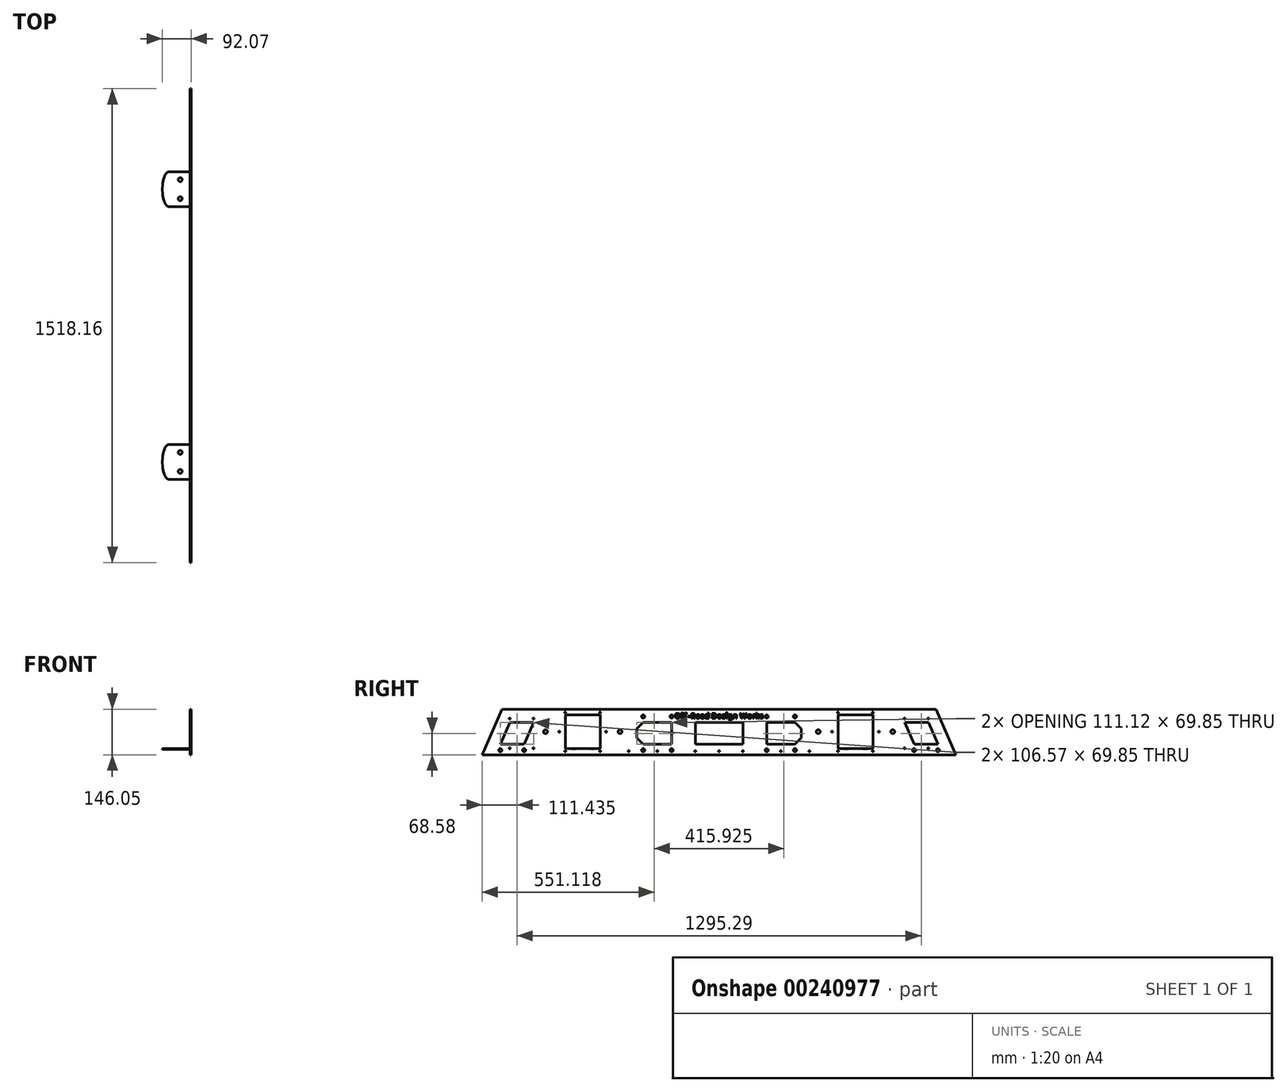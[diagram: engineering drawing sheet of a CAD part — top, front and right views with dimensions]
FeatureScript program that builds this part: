
annotation { "Feature Type Name" : "Feature", "Feature Type Description" : "" }
export const myFeature = defineFeature(function(context is Context, id is Id, definition is map)
    precondition{}
    {
        {
            var Q0;
            Q0=qCreatedBy(makeId("Right.planeOp"),FACE);
            var sketch = newSketch(context, id + "F0", { "sketchPlane" : qUnion([Q0])});
            skLineSegment(sketch, "E0", {"start": v(0, 0) * mm, "end": v(-759.08, 0) * mm});
            skLineSegment(sketch, "E1", {"start": v(-759.08, 0) * mm, "end": v(-695.58, 146.05) * mm});
            skLineSegment(sketch, "E2", {"start": v(-695.58, 146.05) * mm, "end": v(0, 146.05) * mm});
            skLineSegment(sketch, "E3", {"start": v(0, 0) * mm, "end": v(0, 460.36) * mm, "construction": true});
            skLineSegment(sketch, "E4.MirrorCS", {"start": v(695.58, 146.05) * mm, "end": v(0, 146.05) * mm});
            skLineSegment(sketch, "E5.MirrorCS", {"start": v(759.08, 0) * mm, "end": v(695.58, 146.05) * mm});
            skLineSegment(sketch, "E6.MirrorCS", {"start": v(0, 0) * mm, "end": v(759.08, 0) * mm});
            skSolve(sketch);
        }
        {
            var Q0;
            Q0 = qSketchRegion(id + "F0", true);
            extrude(context, id + "F1", {"entities" : qUnion([Q0]), "oppositeDirection" : true, "depth" : 3.17 * mm});
        }
        {
            var Q0;
            Q0=makeQuery(id+"F1.opExtrude","CAP_FACE",FACE,{"disambiguationData":[OSD([sQuery(id+"F0.wireOp",EDGE,"E0"),sQuery(id+"F0.wireOp",EDGE,"E1"),sQuery(id+"F0.wireOp",EDGE,"E2"),sQuery(id+"F0.wireOp",EDGE,"E4.MirrorCS"),sQuery(id+"F0.wireOp",EDGE,"E5.MirrorCS"),sQuery(id+"F0.wireOp",EDGE,"E6.MirrorCS")])],"isStart":true});
            var sketch = newSketch(context, id + "F2", { "sketchPlane" : qUnion([Q0])});
            skLineSegment(sketch, "E7", {"start": v(0, 0) * mm, "end": v(0, 457.35) * mm, "construction": true});
            skLineSegment(sketch, "E8.bottom", {"start": v(-492.76, 127.5) * mm, "end": v(-381, 127.5) * mm});
            skLineSegment(sketch, "E8.top", {"start": v(-492.76, 20.32) * mm, "end": v(-381, 20.32) * mm});
            skLineSegment(sketch, "E8.left", {"start": v(-492.76, 127.5) * mm, "end": v(-492.76, 20.32) * mm});
            skLineSegment(sketch, "E8.right", {"start": v(-381, 127.5) * mm, "end": v(-381, 20.32) * mm});
            skLineSegment(sketch, "E9", {"start": v(-594.36, 103.5) * mm, "end": v(-670.56, 103.5) * mm});
            skLineSegment(sketch, "E10", {"start": v(-670.56, 103.5) * mm, "end": v(-700.93, 33.65) * mm});
            skLineSegment(sketch, "E11", {"start": v(-700.93, 33.65) * mm, "end": v(-624.73, 33.65) * mm});
            skLineSegment(sketch, "E12", {"start": v(-624.73, 33.65) * mm, "end": v(-594.36, 103.5) * mm});
            skArc(sketch, "E13.cCircle", {"start": v(-228.6, 103.5) * mm, "mid": v(-263.53, 68.58) * mm, "end": v(-228.6, 33.65) * mm, "construction": true});
            skLineSegment(sketch, "E13.0", {"start": v(-243.07, 103.5) * mm, "end": v(-214.13, 103.5) * mm});
            skLineSegment(sketch, "E13.4", {"start": v(-214.13, 33.65) * mm, "end": v(-243.07, 33.65) * mm});
            skLineSegment(sketch, "E13.5", {"start": v(-243.07, 33.65) * mm, "end": v(-263.53, 54.11) * mm});
            skLineSegment(sketch, "E13.6", {"start": v(-263.53, 54.11) * mm, "end": v(-263.53, 83.05) * mm});
            skLineSegment(sketch, "E13.7", {"start": v(-263.53, 83.05) * mm, "end": v(-243.07, 103.5) * mm});
            skPoint(sketch, "E13.0.midPoint", {"position": v(-228.6, 103.5) * mm});
            skLineSegment(sketch, "E14", {"start": v(-228.6, 33.65) * mm, "end": v(-152.4, 33.65) * mm});
            skLineSegment(sketch, "E15.MirrorCS", {"start": v(492.76, 127.5) * mm, "end": v(381, 127.5) * mm});
            skLineSegment(sketch, "E16.MirrorCS", {"start": v(492.76, 20.32) * mm, "end": v(381, 20.32) * mm});
            skLineSegment(sketch, "E17.MirrorCS", {"start": v(492.76, 127.5) * mm, "end": v(492.76, 20.32) * mm});
            skLineSegment(sketch, "E18.MirrorCS", {"start": v(381, 127.5) * mm, "end": v(381, 20.32) * mm});
            skLineSegment(sketch, "E19.MirrorCS", {"start": v(594.36, 103.5) * mm, "end": v(670.56, 103.5) * mm});
            skLineSegment(sketch, "E20.MirrorCS", {"start": v(670.56, 103.5) * mm, "end": v(700.93, 33.66) * mm});
            skLineSegment(sketch, "E21.MirrorCS", {"start": v(700.93, 33.65) * mm, "end": v(624.73, 33.65) * mm});
            skLineSegment(sketch, "E22.MirrorCS", {"start": v(624.73, 33.65) * mm, "end": v(594.36, 103.5) * mm});
            skLineSegment(sketch, "E23.MirrorCS", {"start": v(263.53, 54.11) * mm, "end": v(263.53, 83.05) * mm});
            skLineSegment(sketch, "E24.MirrorCS", {"start": v(263.53, 83.05) * mm, "end": v(243.07, 103.5) * mm});
            skArc(sketch, "E25.MirrorCS", {"start": v(228.6, 103.5) * mm, "mid": v(263.53, 68.58) * mm, "end": v(228.6, 33.65) * mm, "construction": true});
            skLineSegment(sketch, "E26.MirrorCS", {"start": v(243.07, 33.65) * mm, "end": v(263.53, 54.11) * mm});
            skLineSegment(sketch, "E27.MirrorCS", {"start": v(214.13, 33.65) * mm, "end": v(243.07, 33.65) * mm});
            skLineSegment(sketch, "E28.MirrorCS", {"start": v(243.07, 103.5) * mm, "end": v(214.13, 103.5) * mm});
            skLineSegment(sketch, "E29.MirrorCS", {"start": v(0, 103.5) * mm, "end": v(76.2, 103.5) * mm});
            skLineSegment(sketch, "E30.MirrorCS", {"start": v(228.6, 33.65) * mm, "end": v(152.4, 33.65) * mm});
            skLineSegment(sketch, "E31", {"start": v(-114.3, 103.5) * mm, "end": v(-114.3, -30.3) * mm, "construction": true});
            skLineSegment(sketch, "E32", {"start": v(-152.4, 103.5) * mm, "end": v(-152.4, 33.65) * mm});
            skLineSegment(sketch, "E33.MirrorCS", {"start": v(-76.2, 103.5) * mm, "end": v(-76.2, 33.65) * mm});
            skLineSegment(sketch, "E34.trimOffspring", {"start": v(-152.4, 103.5) * mm, "end": v(-228.6, 103.5) * mm});
            skPoint(sketch, "E35.start.orphan", {"position": v(0, 103.5) * mm});
            skLineSegment(sketch, "E36.trimOffspring", {"start": v(-76.2, 33.65) * mm, "end": v(0, 33.65) * mm});
            skLineSegment(sketch, "E37", {"start": v(-76.2, 103.5) * mm, "end": v(0, 103.5) * mm});
            skLineSegment(sketch, "E38", {"start": v(114.3, 103.5) * mm, "end": v(114.3, -63.26) * mm, "construction": true});
            skPoint(sketch, "E38.endSnap0", {"position": v(114.3, 103.5) * mm});
            skLineSegment(sketch, "E39", {"start": v(152.4, 103.5) * mm, "end": v(152.4, 33.65) * mm});
            skLineSegment(sketch, "E40.MirrorCS", {"start": v(76.2, 103.5) * mm, "end": v(76.2, 33.65) * mm});
            skLineSegment(sketch, "E41.trimOffspring", {"start": v(152.4, 103.5) * mm, "end": v(228.6, 103.5) * mm});
            skLineSegment(sketch, "E42.trimOffspring", {"start": v(76.2, 33.65) * mm, "end": v(0, 33.65) * mm});
            skSolve(sketch);
        }
        {
            var Q0;
            Q0 = qSketchRegion(id + "F2", true);
            var Q1;
            Q1=makeQuery(id+"F1.opExtrude","CAP_FACE",FACE,{"disambiguationData":[OSD([sQuery(id+"F0.wireOp",EDGE,"E0"),sQuery(id+"F0.wireOp",EDGE,"E1"),sQuery(id+"F0.wireOp",EDGE,"E2"),sQuery(id+"F0.wireOp",EDGE,"E4.MirrorCS"),sQuery(id+"F0.wireOp",EDGE,"E5.MirrorCS"),sQuery(id+"F0.wireOp",EDGE,"E6.MirrorCS")])],"isStart":false});
            extrude(context, id + "F3", {"entities" : qUnion([Q0]), "operationType" : NewBodyOperationType.REMOVE, "endBound" : BoundingType.UP_TO_SURFACE, "oppositeDirection" : true, "endBoundEntityFace" : qUnion([Q1]), "depth" : 25.4 * mm});
        }
        {
            var Q0;
            Q0=makeQuery(id+"F1.opExtrude","CAP_FACE",FACE,{"disambiguationData":[OSD([sQuery(id+"F0.wireOp",EDGE,"E0"),sQuery(id+"F0.wireOp",EDGE,"E1"),sQuery(id+"F0.wireOp",EDGE,"E2"),sQuery(id+"F0.wireOp",EDGE,"E4.MirrorCS"),sQuery(id+"F0.wireOp",EDGE,"E5.MirrorCS"),sQuery(id+"F0.wireOp",EDGE,"E6.MirrorCS")])],"isStart":true});
            var sketch = newSketch(context, id + "F4", { "sketchPlane" : qUnion([Q0])});
            skCircle(sketch, "E43", {"center": v(-670.56, 116.2) * mm, "radius": 1.9 * mm});
            skCircle(sketch, "E44", {"center": v(-594.36, 116.2) * mm, "radius": 1.9 * mm});
            skCircle(sketch, "E45", {"center": v(-670.56, 20.95) * mm, "radius": 1.9 * mm});
            skCircle(sketch, "E46", {"center": v(-594.36, 20.95) * mm, "radius": 1.9 * mm});
            skCircle(sketch, "E47", {"center": v(-624.73, 14.6) * mm, "radius": 5.08 * mm});
            skCircle(sketch, "E48", {"center": v(-700.93, 14.6) * mm, "radius": 5.08 * mm});
            skCircle(sketch, "E49", {"center": v(-492.76, 135.13) * mm, "radius": 1.9 * mm});
            skCircle(sketch, "E50", {"center": v(-381, 135.13) * mm, "radius": 1.9 * mm});
            skLineSegment(sketch, "E51", {"start": v(-492.76, 73.91) * mm, "end": v(-416.14, 73.91) * mm, "construction": true});
            skCircle(sketch, "E52", {"center": v(-492.76, 11.43) * mm, "radius": 1.9 * mm});
            skCircle(sketch, "E53", {"center": v(-381, 11.43) * mm, "radius": 1.9 * mm});
            skCircle(sketch, "E54", {"center": v(-243.07, 14.6) * mm, "radius": 5.08 * mm});
            skCircle(sketch, "E55", {"center": v(-152.4, 14.6) * mm, "radius": 5.08 * mm});
            skLineSegment(sketch, "E56", {"start": v(-263.53, 68.58) * mm, "end": v(-277.88, 68.58) * mm, "construction": true});
            skCircle(sketch, "E57.MirrorC", {"center": v(-243.07, 122.56) * mm, "radius": 5.08 * mm});
            skCircle(sketch, "E58.MirrorC", {"center": v(-152.4, 122.56) * mm, "radius": 5.08 * mm});
            skLineSegment(sketch, "E59", {"start": v(0, 0) * mm, "end": v(0, -131.47) * mm, "construction": true});
            skCircle(sketch, "E60.MirrorC", {"center": v(152.4, 122.56) * mm, "radius": 5.08 * mm});
            skCircle(sketch, "E61.MirrorC", {"center": v(243.07, 122.56) * mm, "radius": 5.08 * mm});
            skCircle(sketch, "E62.MirrorC", {"center": v(243.07, 14.6) * mm, "radius": 5.08 * mm});
            skCircle(sketch, "E63.MirrorC", {"center": v(152.4, 14.6) * mm, "radius": 5.08 * mm});
            skCircle(sketch, "E64.MirrorC", {"center": v(381, 11.43) * mm, "radius": 1.9 * mm});
            skCircle(sketch, "E65.MirrorC", {"center": v(492.76, 11.43) * mm, "radius": 1.9 * mm});
            skCircle(sketch, "E66.MirrorC", {"center": v(492.76, 135.13) * mm, "radius": 1.9 * mm});
            skCircle(sketch, "E67.MirrorC", {"center": v(381, 135.13) * mm, "radius": 1.9 * mm});
            skCircle(sketch, "E68.MirrorC", {"center": v(594.36, 116.2) * mm, "radius": 1.9 * mm});
            skCircle(sketch, "E69.MirrorC", {"center": v(670.56, 116.2) * mm, "radius": 1.9 * mm});
            skCircle(sketch, "E70.MirrorC", {"center": v(670.56, 20.95) * mm, "radius": 1.9 * mm});
            skCircle(sketch, "E71.MirrorC", {"center": v(594.36, 20.95) * mm, "radius": 1.9 * mm});
            skCircle(sketch, "E72.MirrorC", {"center": v(624.73, 14.6) * mm, "radius": 5.08 * mm});
            skCircle(sketch, "E73.MirrorC", {"center": v(700.93, 14.6) * mm, "radius": 5.08 * mm});
            skCircle(sketch, "E74", {"center": v(-361.95, 73.91) * mm, "radius": 1.9 * mm});
            skPoint(sketch, "E74.centerSnap0", {"position": v(-381, 73.91) * mm});
            skCircle(sketch, "E75", {"center": v(-511.81, 73.91) * mm, "radius": 1.9 * mm});
            skCircle(sketch, "E76.MirrorC", {"center": v(361.95, 73.91) * mm, "radius": 1.9 * mm});
            skCircle(sketch, "E77.MirrorC", {"center": v(511.81, 73.91) * mm, "radius": 1.9 * mm});
            skCircle(sketch, "E78", {"center": v(-197.73, 11.43) * mm, "radius": 1.9 * mm});
            skPoint(sketch, "E78.centerSnap0", {"position": v(-197.73, 33.66) * mm});
            skCircle(sketch, "E79", {"center": v(-289.37, 11.43) * mm, "radius": 1.9 * mm});
            skCircle(sketch, "E80.MirrorC", {"center": v(197.73, 11.43) * mm, "radius": 1.9 * mm});
            skCircle(sketch, "E81.MirrorC", {"center": v(289.37, 11.43) * mm, "radius": 1.9 * mm});
            skCircle(sketch, "E82", {"center": v(-76.2, 11.43) * mm, "radius": 1.9 * mm});
            skCircle(sketch, "E83", {"center": v(0, 11.43) * mm, "radius": 1.9 * mm});
            skPoint(sketch, "E83.centerSnap0", {"position": v(0, 33.66) * mm});
            skCircle(sketch, "E84", {"center": v(76.2, 11.43) * mm, "radius": 1.9 * mm});
            skCircle(sketch, "E85", {"center": v(-317.5, 73.91) * mm, "radius": 6.35 * mm});
            skCircle(sketch, "E86", {"center": v(-556.26, 73.91) * mm, "radius": 6.35 * mm});
            skCircle(sketch, "E87.MirrorC", {"center": v(317.5, 73.91) * mm, "radius": 6.35 * mm});
            skCircle(sketch, "E88.MirrorC", {"center": v(556.26, 73.91) * mm, "radius": 6.35 * mm});
            skSolve(sketch);
        }
        {
            var Q0;
            Q0 = qSketchRegion(id + "F4", true);
            var Q1;
            Q1=makeQuery(id+"F1.opExtrude","CAP_FACE",FACE,{"disambiguationData":[OSD([sQuery(id+"F0.wireOp",EDGE,"E0"),sQuery(id+"F0.wireOp",EDGE,"E1"),sQuery(id+"F0.wireOp",EDGE,"E2"),sQuery(id+"F0.wireOp",EDGE,"E4.MirrorCS"),sQuery(id+"F0.wireOp",EDGE,"E5.MirrorCS"),sQuery(id+"F0.wireOp",EDGE,"E6.MirrorCS")])],"isStart":false});
            extrude(context, id + "F5", {"entities" : qUnion([Q0]), "operationType" : NewBodyOperationType.REMOVE, "endBound" : BoundingType.UP_TO_SURFACE, "oppositeDirection" : true, "endBoundEntityFace" : qUnion([Q1]), "depth" : 25.4 * mm});
        }
        {
            var Q0;
            Q0=makeQuery(id+"F1.opExtrude","CAP_FACE",FACE,{"disambiguationData":[OSD([sQuery(id+"F0.wireOp",EDGE,"E0"),sQuery(id+"F0.wireOp",EDGE,"E1"),sQuery(id+"F0.wireOp",EDGE,"E2"),sQuery(id+"F0.wireOp",EDGE,"E4.MirrorCS"),sQuery(id+"F0.wireOp",EDGE,"E5.MirrorCS"),sQuery(id+"F0.wireOp",EDGE,"E6.MirrorCS")])],"isStart":true});
            var sketch = newSketch(context, id + "F6", { "sketchPlane" : qUnion([Q0])});
            skText(sketch, "E89", { "text": "Off-Road Design Works", "fontName": "AllertaStencil-Regular.ttf"});
            skLineSegment(sketch, "E90", {"start": v(0, 0) * mm, "end": v(0, -60.67) * mm, "construction": true});
            skLineSegment(sketch, "E91", {"start": v(0, 116.2) * mm, "end": v(0, 0) * mm, "construction": true});
            const initialGuessF6  = {"E89": [-0.14224, 0.1162, 1, 0, 0.01718]};
            skSetInitialGuess(sketch, initialGuessF6);
            skSolve(sketch);
        }
        {
            var Q0;
            Q0 = qSketchRegion(id + "F6", true);
            var Q1;
            Q1=makeQuery(id+"F1.opExtrude","CAP_FACE",FACE,{"disambiguationData":[OSD([sQuery(id+"F0.wireOp",EDGE,"E0"),sQuery(id+"F0.wireOp",EDGE,"E1"),sQuery(id+"F0.wireOp",EDGE,"E2"),sQuery(id+"F0.wireOp",EDGE,"E4.MirrorCS"),sQuery(id+"F0.wireOp",EDGE,"E5.MirrorCS"),sQuery(id+"F0.wireOp",EDGE,"E6.MirrorCS")])],"isStart":false});
            extrude(context, id + "F7", {"entities" : qUnion([Q0]), "operationType" : NewBodyOperationType.REMOVE, "endBound" : BoundingType.UP_TO_SURFACE, "oppositeDirection" : true, "endBoundEntityFace" : qUnion([Q1]), "depth" : 25.4 * mm});
        }
        {
            var Q0;
            Q0=makeQuery(id+"F3.boolean.opBoolean","COPY",FACE,{"derivedFrom":makeQuery(id+"F3.opExtrude","SWEPT_FACE",FACE,{"disambiguationData":[OSD([sQuery(id+"F2.wireOp",EDGE,"E8.top")])]})});
            var sketch = newSketch(context, id + "F8", { "sketchPlane" : qUnion([Q0])});
            skLineSegment(sketch, "E92", {"start": v(-3.18, -436.88) * mm, "end": v(-45.3, -436.88) * mm, "construction": true});
            skLineSegment(sketch, "E93", {"start": v(-3.18, -492.76) * mm, "end": v(-71.76, -492.76) * mm});
            skLineSegment(sketch, "E94.MirrorCS", {"start": v(-3.18, -381) * mm, "end": v(-71.76, -381) * mm});
            skEllipticalArc(sketch, "E95", {});
            skLineSegment(sketch, "E96", {"start": v(-3.18, -492.76) * mm, "end": v(-3.18, -381) * mm});
            skCircle(sketch, "E97", {"center": v(-34.93, -467.36) * mm, "radius": 6.35 * mm});
            skCircle(sketch, "E98.MirrorC", {"center": v(-34.93, -406.4) * mm, "radius": 6.35 * mm});
            skLineSegment(sketch, "E99", {"start": v(0, 0) * mm, "end": v(-238.43, 0) * mm, "construction": true});
            skLineSegment(sketch, "E100.MirrorCS", {"start": v(-3.18, 381) * mm, "end": v(-71.76, 381) * mm});
            skEllipticalArc(sketch, "E101.MirrorCS", {});
            skCircle(sketch, "E102.MirrorC", {"center": v(-34.93, 406.4) * mm, "radius": 6.35 * mm});
            skCircle(sketch, "E103.MirrorC", {"center": v(-34.93, 467.36) * mm, "radius": 6.35 * mm});
            skLineSegment(sketch, "E104.MirrorCS", {"start": v(-3.18, 492.76) * mm, "end": v(-71.76, 492.76) * mm});
            skLineSegment(sketch, "E105.MirrorCS", {"start": v(-3.18, 492.76) * mm, "end": v(-3.18, 381) * mm});
            const initialGuessF8  = {"E95": [-0.071755, -0.43688, 0, -1, 0.05588, 0.02032, 3.141592653589793, 0], "E101.MirrorCS": [-0.071755, 0.43688, 0, 1, 0.05588, 0.02032, 0, 3.141592653589793]};
            skSetInitialGuess(sketch, initialGuessF8);
            skSolve(sketch);
        }
        {
            var Q0;
            Q0 = qSketchRegion(id + "F8", true);
            extrude(context, id + "F9", {"entities" : qUnion([Q0]), "operationType" : NewBodyOperationType.ADD, "oppositeDirection" : true, "depth" : 3.17 * mm});
        }
    });
